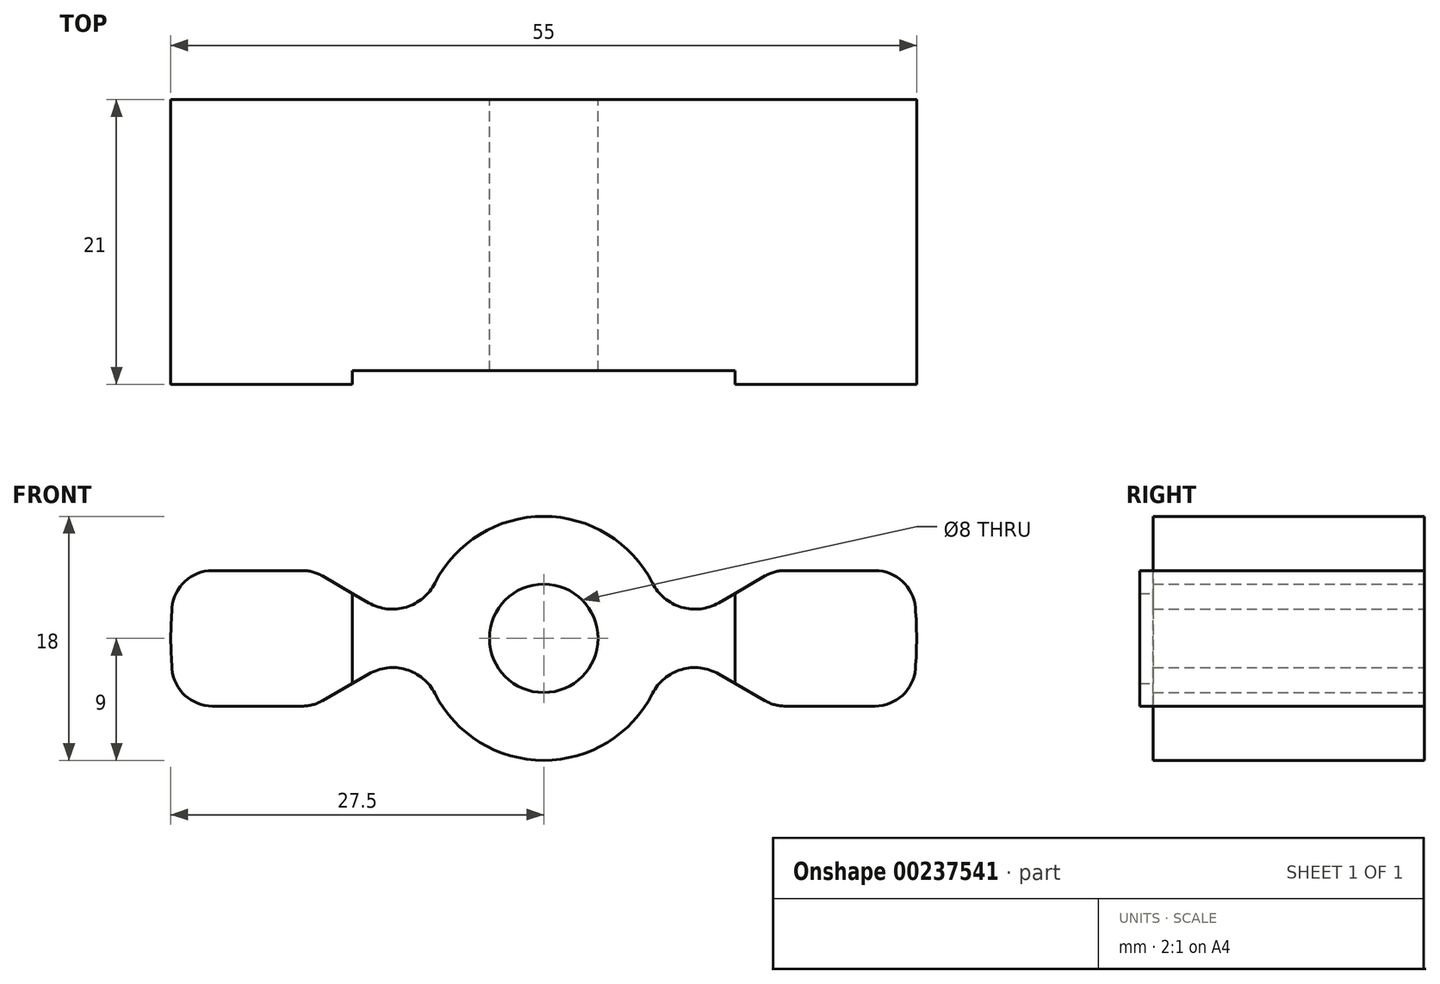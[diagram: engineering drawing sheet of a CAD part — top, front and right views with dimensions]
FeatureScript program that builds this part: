
annotation { "Feature Type Name" : "Feature", "Feature Type Description" : "" }
export const myFeature = defineFeature(function(context is Context, id is Id, definition is map)
    precondition{}
    {
        {
            var Q0;
            Q0=qCreatedBy(makeId("Front.planeOp"),FACE);
            var sketch = newSketch(context, id + "F0", { "sketchPlane" : qUnion([Q0])});
            skArc(sketch, "E0", {"start": v(-8.03, -4.07) * mm, "mid": v(0, -9) * mm, "end": v(8.03, -4.07) * mm});
            skCircle(sketch, "E1", {"center": v(0, 0) * mm, "radius": 4 * mm});
            skLineSegment(sketch, "E2", {"start": v(-12.9, 2.62) * mm, "end": v(-16.32, 4.6) * mm});
            skPoint(sketch, "E3.visualSharp", {"position": v(-9, 0.37) * mm});
            skPoint(sketch, "E4.visualSharp", {"position": v(-27.55, 5) * mm});
            skPoint(sketch, "E5.right.end.orphan", {"position": v(-25, -2) * mm});
            skPoint(sketch, "E5.right.start.orphan", {"position": v(-25, 2) * mm});
            skPoint(sketch, "E6.MirrorP", {"position": v(-9, -0.37) * mm});
            skPoint(sketch, "E7.MirrorP", {"position": v(-27.55, -5) * mm});
            skLineSegment(sketch, "E8.MirrorCS", {"start": v(-12.9, -2.62) * mm, "end": v(-16.32, -4.6) * mm});
            skArc(sketch, "E9.MirrorCS", {"start": v(-12.9, -2.62) * mm, "mid": v(-10.15, -2.3) * mm, "end": v(-8.03, -4.07) * mm});
            skPoint(sketch, "E10.visualSharp", {"position": v(-17.01, 5) * mm});
            skArc(sketch, "E10.filletArc", {"start": v(-16.32, 4.6) * mm, "mid": v(-17.04, 4.9) * mm, "end": v(-17.82, 5) * mm});
            skPoint(sketch, "E11.visualSharp", {"position": v(-17.01, -5) * mm});
            skArc(sketch, "E11.filletArc", {"start": v(-17.82, -5) * mm, "mid": v(-17.04, -4.9) * mm, "end": v(-16.32, -4.6) * mm});
            skLineSegment(sketch, "E12", {"start": v(0, 0) * mm, "end": v(0, 20.65) * mm, "construction": true});
            skArc(sketch, "E13.MirrorCS", {"start": v(-17.82, 5) * mm, "mid": v(-17.04, 4.9) * mm, "end": v(-16.32, 4.6) * mm});
            skArc(sketch, "E14.MirrorCS", {"start": v(-16.32, -4.6) * mm, "mid": v(-17.04, -4.9) * mm, "end": v(-17.82, -5) * mm});
            skLineSegment(sketch, "E15.MirrorCS", {"start": v(-17.82, 5) * mm, "end": v(-24.42, 5) * mm});
            skLineSegment(sketch, "E16.MirrorCS", {"start": v(-17.82, -5) * mm, "end": v(-24.42, -5) * mm});
            skArc(sketch, "E17.MirrorCS", {"start": v(-12.9, 2.62) * mm, "mid": v(-10.15, 2.3) * mm, "end": v(-8.03, 4.07) * mm});
            skArc(sketch, "E18.MirrorCS", {"start": v(17.82, -5) * mm, "mid": v(17.04, -4.9) * mm, "end": v(16.32, -4.6) * mm});
            skArc(sketch, "E19.MirrorCS", {"start": v(17.82, 5) * mm, "mid": v(17.04, 4.9) * mm, "end": v(16.32, 4.6) * mm});
            skArc(sketch, "E20.MirrorCS", {"start": v(16.32, 4.6) * mm, "mid": v(17.04, 4.9) * mm, "end": v(17.82, 5) * mm});
            skArc(sketch, "E21.MirrorCS", {"start": v(16.32, -4.6) * mm, "mid": v(17.04, -4.9) * mm, "end": v(17.82, -5) * mm});
            skPoint(sketch, "E22.MirrorP", {"position": v(25, 2) * mm});
            skPoint(sketch, "E23.MirrorP", {"position": v(25, -2) * mm});
            skPoint(sketch, "E24.MirrorP", {"position": v(27.55, 5) * mm});
            skLineSegment(sketch, "E25.MirrorCS", {"start": v(17.82, -5) * mm, "end": v(24.42, -5) * mm});
            skPoint(sketch, "E26.MirrorP", {"position": v(17.01, -5) * mm});
            skPoint(sketch, "E27.MirrorP", {"position": v(27.55, -5) * mm});
            skPoint(sketch, "E28.MirrorP", {"position": v(17.01, 5) * mm});
            skLineSegment(sketch, "E29.MirrorCS", {"start": v(17.82, 5) * mm, "end": v(24.42, 5) * mm});
            skLineSegment(sketch, "E30.MirrorCS", {"start": v(12.9, -2.62) * mm, "end": v(16.32, -4.6) * mm});
            skArc(sketch, "E31.MirrorCS", {"start": v(12.9, -2.62) * mm, "mid": v(10.15, -2.3) * mm, "end": v(8.03, -4.07) * mm});
            skArc(sketch, "E32.MirrorCS", {"start": v(12.9, 2.62) * mm, "mid": v(10.15, 2.3) * mm, "end": v(8.03, 4.07) * mm});
            skLineSegment(sketch, "E33.MirrorCS", {"start": v(12.9, 2.62) * mm, "end": v(16.32, 4.6) * mm});
            skLineSegment(sketch, "E34.MirrorCS", {"start": v(17.82, -5) * mm, "end": v(24.92, -5) * mm});
            skArc(sketch, "E35.trimOffspring", {"start": v(8.03, 4.07) * mm, "mid": v(0, 9) * mm, "end": v(-8.03, 4.07) * mm});
            skArc(sketch, "E36", {"start": v(-27.4, 2.24) * mm, "mid": v(-27.5, 0) * mm, "end": v(-27.4, -2.24) * mm});
            skPoint(sketch, "E37.orphan", {"position": v(-24.92, 5) * mm});
            skPoint(sketch, "E38.orphan", {"position": v(-24.92, -5) * mm});
            skPoint(sketch, "E39.orphan", {"position": v(24.92, 5) * mm});
            skArc(sketch, "E40.trimOffspring", {"start": v(27.4, -2.24) * mm, "mid": v(27.5, 0) * mm, "end": v(27.4, 2.24) * mm});
            skPoint(sketch, "E41.visualSharp", {"position": v(-27.04, 5) * mm});
            skArc(sketch, "E41.filletArc", {"start": v(-24.42, 5) * mm, "mid": v(-26.45, 4.2) * mm, "end": v(-27.4, 2.24) * mm});
            skPoint(sketch, "E42.visualSharp", {"position": v(-27.04, -5) * mm});
            skArc(sketch, "E42.filletArc", {"start": v(-27.4, -2.24) * mm, "mid": v(-26.45, -4.2) * mm, "end": v(-24.42, -5) * mm});
            skPoint(sketch, "E43.visualSharp", {"position": v(27.04, 5) * mm});
            skArc(sketch, "E43.filletArc", {"start": v(27.4, 2.24) * mm, "mid": v(26.45, 4.2) * mm, "end": v(24.42, 5) * mm});
            skPoint(sketch, "E44.visualSharp", {"position": v(27.04, -5) * mm});
            skArc(sketch, "E44.filletArc", {"start": v(24.42, -5) * mm, "mid": v(26.45, -4.2) * mm, "end": v(27.4, -2.24) * mm});
            skSolve(sketch);
        }
        {
            var Q0;
            Q0=makeQuery(id+"F0.imprint","IMPRINT",FACE,{"disambiguationData":[TD([[makeQuery(id+"F0.imprint","IMPRINT",EDGE,{"derivedFrom":sQuery(id+"F0.wireOp",EDGE,"E0")}),1.0]])]});
            extrude(context, id + "F1", {"entities" : qUnion([Q0]), "depth" : 20 * mm, "symmetric" : true});
        }
        {
            var Q0;
            Q0=makeQuery(id+"F1.opExtrude","CAP_FACE",FACE,{"disambiguationData":[OSD([sQuery(id+"F0.wireOp",EDGE,"E0"),sQuery(id+"F0.wireOp",EDGE,"E1"),sQuery(id+"F0.wireOp",EDGE,"E13.MirrorCS"),sQuery(id+"F0.wireOp",EDGE,"E14.MirrorCS"),sQuery(id+"F0.wireOp",EDGE,"690e1f5a-efa8-4082-a36d-3de76f5ac03c3.MirrorCS"),sQuery(id+"F0.wireOp",EDGE,"690e1f5a-efa8-4082-a36d-3de76f5ac03c4.MirrorCS"),sQuery(id+"F0.wireOp",EDGE,"E15.MirrorCS"),sQuery(id+"F0.wireOp",EDGE,"690e1f5a-efa8-4082-a36d-3de76f5ac03c6.MirrorCS"),sQuery(id+"F0.wireOp",EDGE,"690e1f5a-efa8-4082-a36d-3de76f5ac03c7.MirrorCS"),sQuery(id+"F0.wireOp",EDGE,"E16.MirrorCS"),sQuery(id+"F0.wireOp",EDGE,"E141.MirrorCS"),sQuery(id+"F0.wireOp",EDGE,"E142.MirrorCS"),sQuery(id+"F0.wireOp",EDGE,"E17.MirrorCS"),sQuery(id+"F0.wireOp",EDGE,"E147.MirrorCS"),sQuery(id+"F0.wireOp",EDGE,"E20.MirrorCS"),sQuery(id+"F0.wireOp",EDGE,"59a6e838-1b82-4cbb-bfe9-611c24104aca5.MirrorCS"),sQuery(id+"F0.wireOp",EDGE,"59a6e838-1b82-4cbb-bfe9-611c24104aca6.MirrorCS"),sQuery(id+"F0.wireOp",EDGE,"E21.MirrorCS"),sQuery(id+"F0.wireOp",EDGE,"E185.MirrorCS"),sQuery(id+"F0.wireOp",EDGE,"E31.MirrorCS"),sQuery(id+"F0.wireOp",EDGE,"E187.MirrorCS"),sQuery(id+"F0.wireOp",EDGE,"E32.MirrorCS"),sQuery(id+"F0.wireOp",EDGE,"E189.MirrorCS"),sQuery(id+"F0.wireOp",EDGE,"E33.MirrorCS"),sQuery(id+"F0.wireOp",EDGE,"E34.MirrorCS"),sQuery(id+"F0.wireOp",EDGE,"E197.MirrorCS"),sQuery(id+"F0.wireOp",EDGE,"E35.trimOffspring")])],"isStart":false});
            var sketch = newSketch(context, id + "F2", { "sketchPlane" : qUnion([Q0])});
            skLineSegment(sketch, "E45.0", {"start": v(-17.82, 5) * mm, "end": v(-17.82, 5) * mm});
            skLineSegment(sketch, "E45.4", {"start": v(-17.82, -5) * mm, "end": v(-24.92, -5) * mm});
            skArc(sketch, "E45.5", {"start": v(-17.82, 5) * mm, "mid": v(-17.04, 4.9) * mm, "end": v(-16.32, 4.6) * mm});
            skLineSegment(sketch, "E45.6", {"start": v(-14.1, 3.32) * mm, "end": v(-16.32, 4.6) * mm});
            skArc(sketch, "E45.8", {"start": v(-16.32, -4.6) * mm, "mid": v(-17.04, -4.9) * mm, "end": v(-17.82, -5) * mm});
            skLineSegment(sketch, "E45.9", {"start": v(-14.1, -3.32) * mm, "end": v(-16.32, -4.6) * mm});
            skLineSegment(sketch, "E46", {"start": v(-14.1, 3.32) * mm, "end": v(-14.1, -3.32) * mm});
            skPoint(sketch, "E45.10.end.orphan", {"position": v(-8.03, -4.07) * mm});
            skPoint(sketch, "E45.10.start.orphan", {"position": v(-12.9, -2.62) * mm});
            skPoint(sketch, "E45.7.end.orphan", {"position": v(-8.03, 4.07) * mm});
            skPoint(sketch, "E45.7.start.orphan", {"position": v(-12.9, 2.62) * mm});
            skArc(sketch, "E47.0", {"start": v(-27.4, -2.24) * mm, "mid": v(-26.45, -4.2) * mm, "end": v(-24.42, -5) * mm});
            skArc(sketch, "E47.1", {"start": v(-27.4, 2.24) * mm, "mid": v(-27.5, 0) * mm, "end": v(-27.4, -2.24) * mm});
            skArc(sketch, "E47.2", {"start": v(-24.42, 5) * mm, "mid": v(-26.45, 4.2) * mm, "end": v(-27.4, 2.24) * mm});
            skLineSegment(sketch, "E47.3", {"start": v(-17.82, 5) * mm, "end": v(-24.42, 5) * mm});
            skLineSegment(sketch, "E48", {"start": v(0, 0) * mm, "end": v(0, 15.66) * mm, "construction": true});
            skArc(sketch, "E49.MirrorCS", {"start": v(16.32, -4.6) * mm, "mid": v(17.04, -4.9) * mm, "end": v(17.82, -5) * mm});
            skArc(sketch, "E50.MirrorCS", {"start": v(17.82, 5) * mm, "mid": v(17.04, 4.9) * mm, "end": v(16.32, 4.6) * mm});
            skLineSegment(sketch, "E51.MirrorCS", {"start": v(14.1, 3.32) * mm, "end": v(16.32, 4.6) * mm});
            skPoint(sketch, "E52.MirrorP", {"position": v(12.9, -2.62) * mm});
            skLineSegment(sketch, "E53.MirrorCS", {"start": v(14.1, 3.32) * mm, "end": v(14.1, -3.32) * mm});
            skArc(sketch, "E54.MirrorCS", {"start": v(27.4, 2.24) * mm, "mid": v(27.5, 0) * mm, "end": v(27.4, -2.24) * mm});
            skLineSegment(sketch, "E55.MirrorCS", {"start": v(17.82, -5) * mm, "end": v(24.92, -5) * mm});
            skLineSegment(sketch, "E56.MirrorCS", {"start": v(14.1, -3.32) * mm, "end": v(16.32, -4.6) * mm});
            skLineSegment(sketch, "E57.MirrorCS", {"start": v(17.82, 5) * mm, "end": v(24.42, 5) * mm});
            skArc(sketch, "E58.MirrorCS", {"start": v(24.42, 5) * mm, "mid": v(26.45, 4.2) * mm, "end": v(27.4, 2.24) * mm});
            skPoint(sketch, "E59.MirrorP", {"position": v(12.9, 2.62) * mm});
            skArc(sketch, "E60.MirrorCS", {"start": v(27.4, -2.24) * mm, "mid": v(26.45, -4.2) * mm, "end": v(24.42, -5) * mm});
            skSolve(sketch);
        }
        {
            var Q0;
            Q0 = qSketchRegion(id + "F2", true);
            extrude(context, id + "F3", {"entities" : qUnion([Q0]), "operationType" : NewBodyOperationType.ADD, "depth" : 1 * mm});
        }
    });
